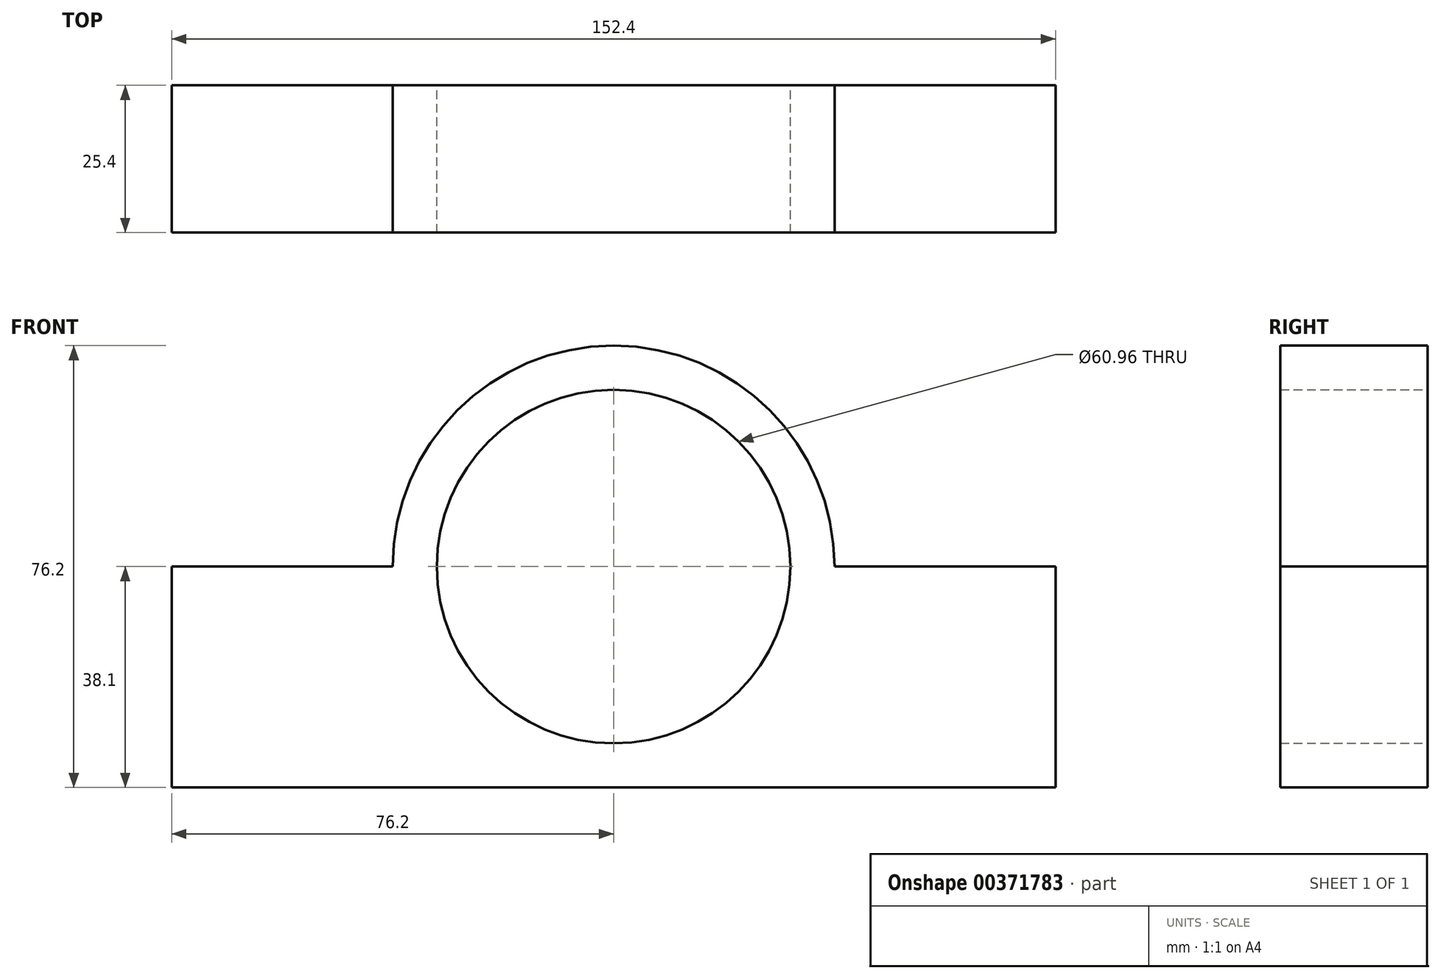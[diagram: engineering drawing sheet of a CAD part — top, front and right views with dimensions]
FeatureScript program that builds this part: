
annotation { "Feature Type Name" : "Feature", "Feature Type Description" : "" }
export const myFeature = defineFeature(function(context is Context, id is Id, definition is map)
    precondition{}
    {
        {
            var Q0;
            Q0=qCreatedBy(makeId("Front.planeOp"),FACE);
            var sketch = newSketch(context, id + "F0", { "sketchPlane" : qUnion([Q0])});
            skArc(sketch, "E0", {"start": v(38.1, 0) * mm, "mid": v(0, 38.1) * mm, "end": v(-38.1, 0) * mm});
            skLineSegment(sketch, "E1", {"start": v(-38.1, 0) * mm, "end": v(-76.2, 0) * mm});
            skLineSegment(sketch, "E2", {"start": v(-76.2, 0) * mm, "end": v(-76.2, -38.1) * mm});
            skLineSegment(sketch, "E3", {"start": v(-76.2, -38.1) * mm, "end": v(76.2, -38.1) * mm});
            skLineSegment(sketch, "E4", {"start": v(76.2, -38.1) * mm, "end": v(76.2, 0) * mm});
            skLineSegment(sketch, "E5", {"start": v(76.2, 0) * mm, "end": v(38.1, 0) * mm});
            skCircle(sketch, "E6", {"center": v(0, 0) * mm, "radius": 30.48 * mm});
            skSolve(sketch);
        }
        {
            var Q0;
            Q0=makeQuery(id+"F0.imprint","IMPRINT",FACE,{"disambiguationData":[TD([[makeQuery(id+"F0.imprint","IMPRINT",EDGE,{"derivedFrom":sQuery(id+"F0.wireOp",EDGE,"E0")}),1.0]])]});
            extrude(context, id + "F1", {"entities" : qUnion([Q0]), "depth" : 25.4 * mm});
        }
    });
